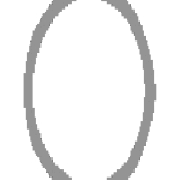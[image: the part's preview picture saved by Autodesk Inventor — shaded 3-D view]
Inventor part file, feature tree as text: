
AUTODESK INVENTOR PART (.ipt)
format: ipt  version: 2021 (Build 250183000, 183)  size: 114,176 bytes
history: native  units: in
note: dims shown in document units (in); Inventor stores cm internally (conversion verified against a paired STEP export)
features: other x4, sketch x3, plane x1
ambient origin geometry x8: Origin, YZ Plane, XZ Plane, XY Plane, X Axis, Y Axis, Z Axis, Center Point
bodies: Solid1 (feature_tree), Body (feature_tree)
feature tree (8):
  other  "Driven Length"
  other  "Frame Generator"
  other  "Start Plane"
  other  "End Plane"
  sketch  "Sketch"  dims[d2=5.831in d4=-0.0in d5=5.831in d6=0.12in d7=0.0in d8=90.0deg d9=5.831in]
  sketch  "Sketch2"  dims[d0=1.0in]
  plane  "Work Plane3"
  sketch  "Sketch3"  dims[d1=0.065in]
